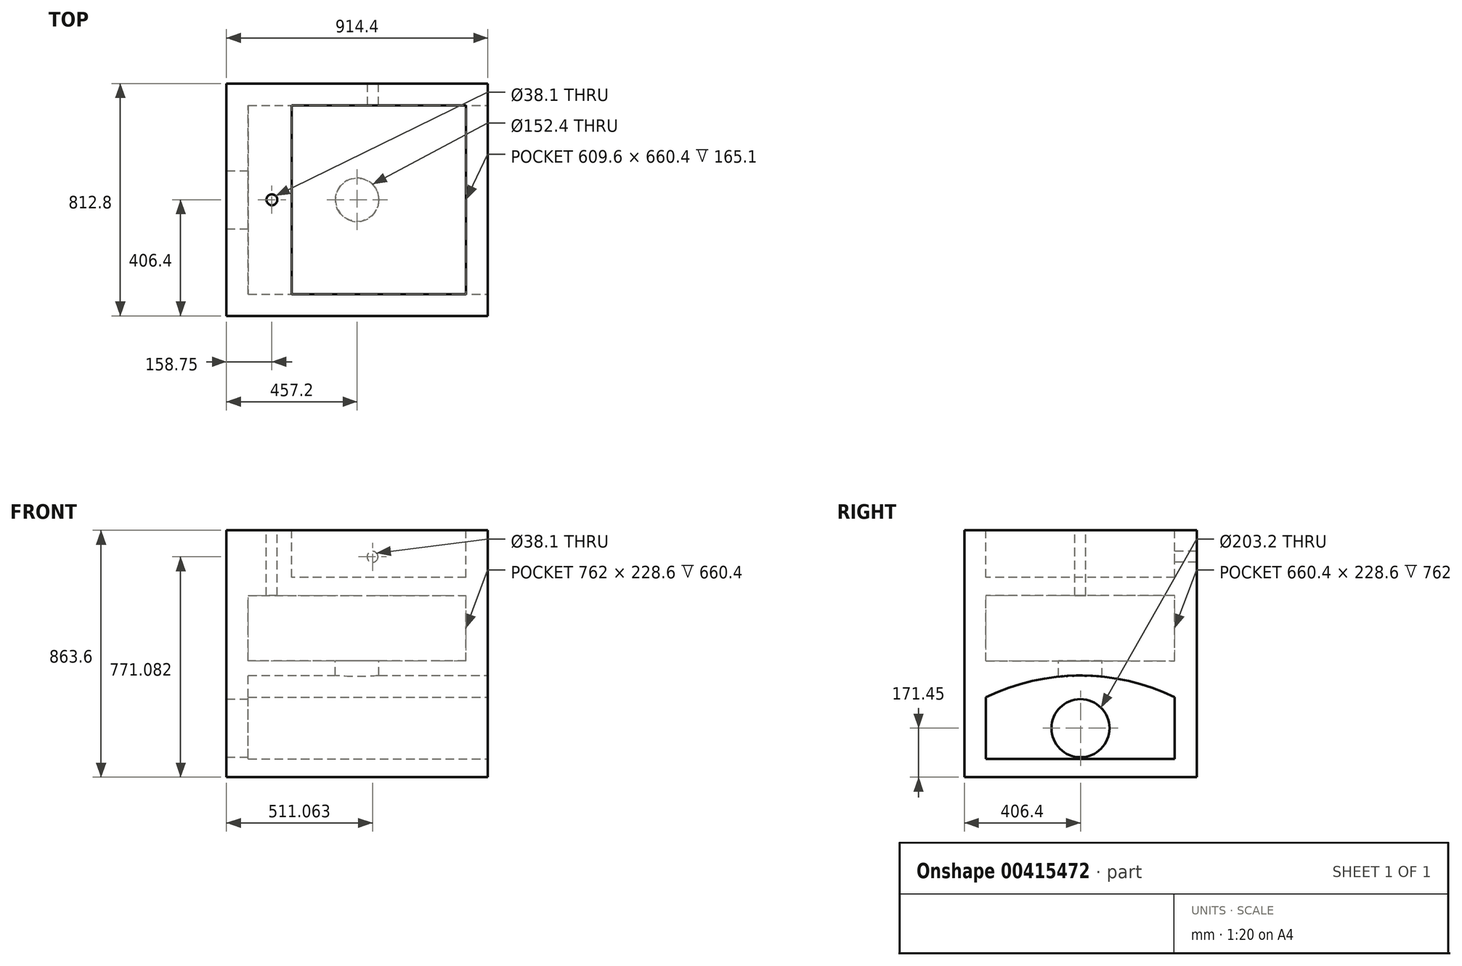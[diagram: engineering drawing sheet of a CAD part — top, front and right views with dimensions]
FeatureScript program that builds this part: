
annotation { "Feature Type Name" : "Feature", "Feature Type Description" : "" }
export const myFeature = defineFeature(function(context is Context, id is Id, definition is map)
    precondition{}
    {
        {
            var Q0;
            Q0=qCreatedBy(makeId("Top.planeOp"),FACE);
            var sketch = newSketch(context, id + "F0", { "sketchPlane" : qUnion([Q0])});
            skLineSegment(sketch, "E0.bottom", {"start": v(457.2, -406.4) * mm, "end": v(-457.2, -406.4) * mm});
            skLineSegment(sketch, "E0.top", {"start": v(457.2, 406.4) * mm, "end": v(-457.2, 406.4) * mm});
            skLineSegment(sketch, "E0.left", {"start": v(457.2, -406.4) * mm, "end": v(457.2, 406.4) * mm});
            skLineSegment(sketch, "E0.right", {"start": v(-457.2, -406.4) * mm, "end": v(-457.2, 406.4) * mm});
            skPoint(sketch, "E0.middle", {"position": v(0, 0) * mm});
            skSolve(sketch);
        }
        {
            var Q0;
            Q0=makeQuery(id+"F0.imprint","IMPRINT",FACE,{"disambiguationData":[TD([[makeQuery(id+"F0.imprint","IMPRINT",EDGE,{"derivedFrom":sQuery(id+"F0.wireOp",EDGE,"E0.bottom")}),-1.0]])]});
            extrude(context, id + "F1", {"entities" : qUnion([Q0]), "depth" : 863.6 * mm});
        }
        {
            var Q0;
            Q0=makeQuery(id+"F1.opExtrude","SWEPT_FACE",FACE,{"disambiguationData":[OSD([sQuery(id+"F0.wireOp",EDGE,"E0.left")])]});
            var sketch = newSketch(context, id + "F2", { "sketchPlane" : qUnion([Q0])});
            skLineSegment(sketch, "E1", {"start": v(-406.4, 431.8) * mm, "end": v(406.4, 431.8) * mm});
            skPoint(sketch, "E2", {"position": v(0, 355.6) * mm});
            skPoint(sketch, "E2.positionSnap0", {"position": v(0, 431.8) * mm});
            skArc(sketch, "E3", {"start": v(330.2, 279.4) * mm, "mid": v(0, 355.6) * mm, "end": v(-330.2, 279.4) * mm});
            skLineSegment(sketch, "E4", {"start": v(-330.2, 279.4) * mm, "end": v(-330.2, 63.5) * mm});
            skLineSegment(sketch, "E5", {"start": v(-330.2, 63.5) * mm, "end": v(330.2, 63.5) * mm});
            skLineSegment(sketch, "E6", {"start": v(330.2, 63.5) * mm, "end": v(330.2, 279.4) * mm});
            skLineSegment(sketch, "E7.bottom", {"start": v(-330.2, 863.6) * mm, "end": v(330.2, 863.6) * mm});
            skLineSegment(sketch, "E7.top", {"start": v(-330.2, 431.8) * mm, "end": v(330.2, 431.8) * mm});
            skLineSegment(sketch, "E7.left", {"start": v(-330.2, 863.6) * mm, "end": v(-330.2, 431.8) * mm});
            skLineSegment(sketch, "E7.right", {"start": v(330.2, 863.6) * mm, "end": v(330.2, 431.8) * mm});
            skLineSegment(sketch, "E8", {"start": v(-330.2, 685.8) * mm, "end": v(330.2, 685.8) * mm});
            skSolve(sketch);
        }
        {
            var Q0;
            Q0=makeQuery(id+"F2.imprint","IMPRINT",FACE,{"disambiguationData":[TD([[makeQuery(id+"F2.imprint","IMPRINT",EDGE,{"derivedFrom":sQuery(id+"F2.wireOp",EDGE,"E3")}),1.0]])]});
            extrude(context, id + "F3", {"entities" : qUnion([Q0]), "operationType" : NewBodyOperationType.REMOVE, "oppositeDirection" : true, "depth" : 838.2 * mm});
        }
        {
            var Q0;
            Q0=makeQuery(id+"F1.opExtrude","CAP_FACE",FACE,{"disambiguationData":[OSD([sQuery(id+"F0.wireOp",EDGE,"E0.bottom"),sQuery(id+"F0.wireOp",EDGE,"E0.top"),sQuery(id+"F0.wireOp",EDGE,"E0.left"),sQuery(id+"F0.wireOp",EDGE,"E0.right")])],"isStart":false});
            var sketch = newSketch(context, id + "F4", { "sketchPlane" : qUnion([Q0])});
            skLineSegment(sketch, "E9.bottom", {"start": v(381, -330.2) * mm, "end": v(-228.6, -330.2) * mm});
            skLineSegment(sketch, "E9.top", {"start": v(381, 330.2) * mm, "end": v(-228.6, 330.2) * mm});
            skLineSegment(sketch, "E9.left", {"start": v(381, -330.2) * mm, "end": v(381, 330.2) * mm});
            skLineSegment(sketch, "E9.right", {"start": v(-228.6, -330.2) * mm, "end": v(-228.6, 330.2) * mm});
            skSolve(sketch);
        }
        {
            var Q0;
            Q0=makeQuery(id+"F4.imprint","IMPRINT",FACE,{"disambiguationData":[TD([[makeQuery(id+"F4.imprint","IMPRINT",EDGE,{"derivedFrom":sQuery(id+"F4.wireOp",EDGE,"E9.bottom")}),-1.0]])]});
            extrude(context, id + "F5", {"entities" : qUnion([Q0]), "operationType" : NewBodyOperationType.REMOVE, "oppositeDirection" : true, "depth" : 457.2 * mm});
        }
        {
            var Q0;
            Q0=makeQuery(id+"F5.boolean.opBoolean","COPY",FACE,{"derivedFrom":makeQuery(id+"F5.opExtrude","SWEPT_FACE",FACE,{"disambiguationData":[OSD([sQuery(id+"F4.wireOp",EDGE,"E9.right")])]})});
            var sketch = newSketch(context, id + "F6", { "sketchPlane" : qUnion([Q0])});
            skLineSegment(sketch, "E10", {"start": v(330.2, 635) * mm, "end": v(-330.2, 635) * mm});
            skSolve(sketch);
        }
        {
            var Q0;
            {var subQ0=sQuery(id+"F6.wireOp",EDGE,"E10");Q0=makeQuery(id+"F6.imprint","IMPRINT",FACE,{"disambiguationData":[TD([[makeQuery(id+"F6.imprint","IMPRINT",EDGE,{"derivedFrom":subQ0}),1.0]])]});}
            extrude(context, id + "F7", {"entities" : qUnion([Q0]), "operationType" : NewBodyOperationType.REMOVE, "oppositeDirection" : true, "depth" : 152.4 * mm});
        }
        {
            var Q0;
            Q0=makeQuery(id+"F1.opExtrude","CAP_FACE",FACE,{"disambiguationData":[OSD([sQuery(id+"F0.wireOp",EDGE,"E0.bottom"),sQuery(id+"F0.wireOp",EDGE,"E0.top"),sQuery(id+"F0.wireOp",EDGE,"E0.left"),sQuery(id+"F0.wireOp",EDGE,"E0.right")])],"isStart":false});
            var sketch = newSketch(context, id + "F8", { "sketchPlane" : qUnion([Q0])});
            skCircle(sketch, "E11", {"center": v(-298.45, 0) * mm, "radius": 19.05 * mm});
            skPoint(sketch, "E11.centerSnap0", {"position": v(-228.6, 0) * mm});
            skSolve(sketch);
        }
        {
            var Q0;
            Q0=makeQuery(id+"F8.imprint","IMPRINT",FACE,{"disambiguationData":[TD([[makeQuery(id+"F8.imprint","IMPRINT",EDGE,{"derivedFrom":sQuery(id+"F8.wireOp",EDGE,"E11")}),1.0]])]});
            extrude(context, id + "F9", {"entities" : qUnion([Q0]), "operationType" : NewBodyOperationType.REMOVE, "endBound" : BoundingType.UP_TO_NEXT, "oppositeDirection" : true, "depth" : 25.4 * mm});
        }
        {
            var Q0;
            Q0=makeQuery(id+"F5.boolean.opBoolean","COPY",FACE,{"derivedFrom":makeQuery(id+"F5.opExtrude","SWEPT_FACE",FACE,{"disambiguationData":[OSD([sQuery(id+"F4.wireOp",EDGE,"E9.right")])]})});
            var sketch = newSketch(context, id + "F10", { "sketchPlane" : qUnion([Q0])});
            skLineSegment(sketch, "E12", {"start": v(330.2, 698.5) * mm, "end": v(-330.2, 698.5) * mm});
            skSolve(sketch);
        }
        {
            var Q0;
            {var subQ0=sQuery(id+"F10.wireOp",EDGE,"E12");Q0=makeQuery(id+"F10.imprint","IMPRINT",FACE,{"disambiguationData":[TD([[makeQuery(id+"F10.imprint","IMPRINT",EDGE,{"derivedFrom":subQ0}),1.0]])]});}
            extrude(context, id + "F11", {"entities" : qUnion([Q0]), "operationType" : NewBodyOperationType.ADD, "endBound" : BoundingType.UP_TO_NEXT, "depth" : 25.4 * mm});
        }
        {
            var Q0;
            {var subQ0=sQuery(id+"F4.wireOp",EDGE,"E9.right");var subQ1=sQuery(id+"F4.wireOp",EDGE,"E9.top");Q0=makeQuery(id+"F11.boolean.opBoolean","SPLIT",FACE,{"disambiguationData":[TD([makeQuery(id+"F5.boolean.opBoolean","COPY",FACE,{"derivedFrom":makeQuery(id+"F5.opExtrude","SWEPT_FACE",FACE,{"disambiguationData":[OSD([subQ0])]})})])],"derivedFrom":makeQuery(id+"F7.boolean.opBoolean","MERGE",FACE,{"derivedFrom":[makeQuery(id+"F5.boolean.opBoolean","COPY",FACE,{"derivedFrom":makeQuery(id+"F5.opExtrude","SWEPT_FACE",FACE,{"disambiguationData":[OSD([subQ1])]})}),makeQuery(id+"F7.opExtrude","SWEPT_FACE",FACE,{"disambiguationData":[OSD([subQ1,subQ0])]})]})});}
            var sketch = newSketch(context, id + "F12", { "sketchPlane" : qUnion([Q0])});
            skCircle(sketch, "E13", {"center": v(53.86, 771.08) * mm, "radius": 19.05 * mm});
            skSolve(sketch);
        }
        {
            var Q0;
            Q0=makeQuery(id+"F12.imprint","IMPRINT",FACE,{"disambiguationData":[TD([[makeQuery(id+"F12.imprint","IMPRINT",EDGE,{"derivedFrom":sQuery(id+"F12.wireOp",EDGE,"E13")}),1.0]])]});
            extrude(context, id + "F13", {"entities" : qUnion([Q0]), "operationType" : NewBodyOperationType.REMOVE, "endBound" : BoundingType.THROUGH_ALL, "oppositeDirection" : true, "depth" : 25.4 * mm});
        }
        {
            var Q0;
            {var subQ0=sQuery(id+"F4.wireOp",EDGE,"E9.right");Q0=makeQuery(id+"F7.boolean.opBoolean","MERGE",FACE,{"derivedFrom":[makeQuery(id+"F5.boolean.opBoolean","COPY",FACE,{"derivedFrom":makeQuery(id+"F5.opExtrude","CAP_FACE",FACE,{"disambiguationData":[OSD([sQuery(id+"F4.wireOp",EDGE,"E9.bottom"),sQuery(id+"F4.wireOp",EDGE,"E9.top"),sQuery(id+"F4.wireOp",EDGE,"E9.left"),subQ0])],"isStart":false})}),makeQuery(id+"F7.opExtrude","SWEPT_FACE",FACE,{"disambiguationData":[OSD([subQ0])]})]});}
            var sketch = newSketch(context, id + "F14", { "sketchPlane" : qUnion([Q0])});
            skCircle(sketch, "E14", {"center": v(0, 0) * mm, "radius": 76.2 * mm});
            skSolve(sketch);
        }
        {
            var Q0;
            Q0=makeQuery(id+"F14.imprint","IMPRINT",FACE,{"disambiguationData":[TD([[makeQuery(id+"F14.imprint","IMPRINT",EDGE,{"derivedFrom":sQuery(id+"F14.wireOp",EDGE,"E14")}),1.0]])]});
            extrude(context, id + "F15", {"entities" : qUnion([Q0]), "operationType" : NewBodyOperationType.REMOVE, "endBound" : BoundingType.UP_TO_NEXT, "oppositeDirection" : true, "depth" : 25.4 * mm});
        }
        {
            var Q0;
            Q0=makeQuery(id+"F3.boolean.opBoolean","COPY",FACE,{"derivedFrom":makeQuery(id+"F3.opExtrude","CAP_FACE",FACE,{"disambiguationData":[OSD([sQuery(id+"F2.wireOp",EDGE,"E3"),sQuery(id+"F2.wireOp",EDGE,"E4"),sQuery(id+"F2.wireOp",EDGE,"E5"),sQuery(id+"F2.wireOp",EDGE,"E6")])],"isStart":false})});
            var sketch = newSketch(context, id + "F16", { "sketchPlane" : qUnion([Q0])});
            skCircle(sketch, "E15", {"center": v(0, 171.45) * mm, "radius": 101.6 * mm});
            skPoint(sketch, "E15.centerSnap0", {"position": v(-330.2, 171.45) * mm});
            skSolve(sketch);
        }
        {
            var Q0;
            Q0=makeQuery(id+"F16.imprint","IMPRINT",FACE,{"disambiguationData":[TD([[makeQuery(id+"F16.imprint","IMPRINT",EDGE,{"derivedFrom":sQuery(id+"F16.wireOp",EDGE,"E15")}),1.0]])]});
            extrude(context, id + "F17", {"entities" : qUnion([Q0]), "operationType" : NewBodyOperationType.REMOVE, "endBound" : BoundingType.THROUGH_ALL, "oppositeDirection" : true, "depth" : 25.4 * mm});
        }
    });
